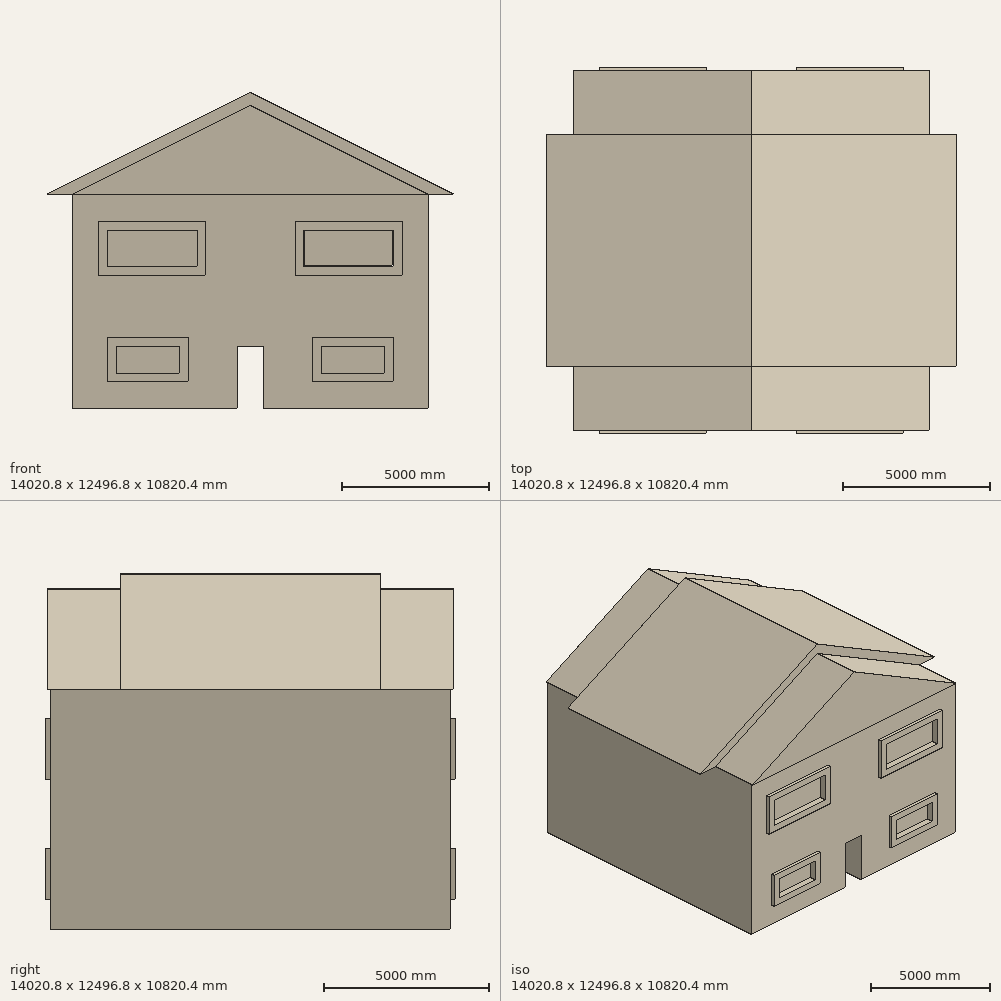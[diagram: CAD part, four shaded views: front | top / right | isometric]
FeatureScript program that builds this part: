
annotation { "Feature Type Name" : "Feature", "Feature Type Description" : "" }
export const myFeature = defineFeature(function(context is Context, id is Id, definition is map)
    precondition{}
    {
        {
            var Q0;
            Q0=qCreatedBy(makeId("Front.planeOp"),FACE);
            var sketch = newSketch(context, id + "F0", { "sketchPlane" : qUnion([Q0])});
            skLineSegment(sketch, "E0", {"start": v(0, 0) * mm, "end": v(-6096, 0) * mm});
            skLineSegment(sketch, "E1", {"start": v(0, 0) * mm, "end": v(6096, 0) * mm});
            skLineSegment(sketch, "E2", {"start": v(0, 0) * mm, "end": v(0, 3048) * mm, "construction": true});
            skLineSegment(sketch, "E3", {"start": v(0, 3048) * mm, "end": v(-6096, 0) * mm});
            skLineSegment(sketch, "E4", {"start": v(0, 3048) * mm, "end": v(6096, 0) * mm});
            skLineSegment(sketch, "E5", {"start": v(-6096, 0) * mm, "end": v(-7010.4, 0) * mm});
            skLineSegment(sketch, "E6", {"start": v(6096, 0) * mm, "end": v(7010.4, 0) * mm});
            skLineSegment(sketch, "E7", {"start": v(0, 3048) * mm, "end": v(0, 3505.2) * mm});
            skLineSegment(sketch, "E8", {"start": v(-7010.4, 0) * mm, "end": v(0, 3505.2) * mm});
            skLineSegment(sketch, "E9", {"start": v(0, 3505.2) * mm, "end": v(7010.4, 0) * mm});
            skLineSegment(sketch, "E10", {"start": v(-6096, 0) * mm, "end": v(-6096, -7315.2) * mm});
            skLineSegment(sketch, "E11", {"start": v(6096, 0) * mm, "end": v(6096, -7315.2) * mm});
            skLineSegment(sketch, "E12", {"start": v(-6096, -7315.2) * mm, "end": v(6096, -7315.2) * mm});
            skLineSegment(sketch, "E13", {"start": v(0, 0) * mm, "end": v(0, -7315.2) * mm, "construction": true});
            skLineSegment(sketch, "E14", {"start": v(0, -7315.2) * mm, "end": v(-457.2, -7315.2) * mm});
            skLineSegment(sketch, "E15", {"start": v(0, -7315.2) * mm, "end": v(457.2, -7315.2) * mm});
            skLineSegment(sketch, "E16", {"start": v(-457.2, -7315.2) * mm, "end": v(-457.2, -5181.6) * mm});
            skLineSegment(sketch, "E17", {"start": v(457.2, -7315.2) * mm, "end": v(457.2, -5181.6) * mm});
            skLineSegment(sketch, "E18", {"start": v(-457.2, -5181.6) * mm, "end": v(457.2, -5181.6) * mm});
            skPoint(sketch, "E19.firstSnap0", {"position": v(0, -5181.6) * mm});
            skLineSegment(sketch, "E19.bottom", {"start": v(2438.4, -5181.6) * mm, "end": v(4572, -5181.6) * mm});
            skLineSegment(sketch, "E19.top", {"start": v(2438.4, -6096) * mm, "end": v(4572, -6096) * mm});
            skLineSegment(sketch, "E19.left", {"start": v(2438.4, -5181.6) * mm, "end": v(2438.4, -6096) * mm});
            skLineSegment(sketch, "E19.right", {"start": v(4572, -5181.6) * mm, "end": v(4572, -6096) * mm});
            skLineSegment(sketch, "E20", {"start": v(-6096, -7315.2) * mm, "end": v(-6096, -7620) * mm});
            skLineSegment(sketch, "E21", {"start": v(6096, -7315.2) * mm, "end": v(6096, -7620) * mm});
            skLineSegment(sketch, "E22", {"start": v(6096, -7620) * mm, "end": v(-6096, -7620) * mm});
            skLineSegment(sketch, "E23.0", {"start": v(2133.6, -4876.8) * mm, "end": v(4876.8, -4876.8) * mm});
            skLineSegment(sketch, "E23.1", {"start": v(2133.6, -4876.8) * mm, "end": v(2133.6, -6400.8) * mm});
            skLineSegment(sketch, "E23.2", {"start": v(2133.6, -6400.8) * mm, "end": v(4876.8, -6400.8) * mm});
            skLineSegment(sketch, "E23.3", {"start": v(4876.8, -4876.8) * mm, "end": v(4876.8, -6400.8) * mm});
            skLineSegment(sketch, "E24.bottom", {"start": v(-4572, -5181.6) * mm, "end": v(-2438.4, -5181.6) * mm});
            skLineSegment(sketch, "E24.top", {"start": v(-4572, -6096) * mm, "end": v(-2438.4, -6096) * mm});
            skLineSegment(sketch, "E24.left", {"start": v(-4572, -5181.6) * mm, "end": v(-4572, -6096) * mm});
            skLineSegment(sketch, "E24.right", {"start": v(-2438.4, -5181.6) * mm, "end": v(-2438.4, -6096) * mm});
            skLineSegment(sketch, "E25.0", {"start": v(-4876.8, -4876.8) * mm, "end": v(-2133.6, -4876.8) * mm});
            skLineSegment(sketch, "E25.1", {"start": v(-4876.8, -4876.8) * mm, "end": v(-4876.8, -6400.8) * mm});
            skLineSegment(sketch, "E25.2", {"start": v(-4876.8, -6400.8) * mm, "end": v(-2133.6, -6400.8) * mm});
            skLineSegment(sketch, "E25.3", {"start": v(-2133.6, -4876.8) * mm, "end": v(-2133.6, -6400.8) * mm});
            skLineSegment(sketch, "E26.bottom", {"start": v(1828.8, -1219.2) * mm, "end": v(4876.8, -1219.2) * mm});
            skLineSegment(sketch, "E26.top", {"start": v(1828.8, -2438.4) * mm, "end": v(4876.8, -2438.4) * mm});
            skLineSegment(sketch, "E26.left", {"start": v(1828.8, -1219.2) * mm, "end": v(1828.8, -2438.4) * mm});
            skLineSegment(sketch, "E26.right", {"start": v(4876.8, -1219.2) * mm, "end": v(4876.8, -2438.4) * mm});
            skLineSegment(sketch, "E27.0", {"start": v(1833.8, -1219.2) * mm, "end": v(1833.8, -2433.4) * mm});
            skLineSegment(sketch, "E27.1", {"start": v(1833.8, -2433.4) * mm, "end": v(4871.8, -2433.4) * mm});
            skLineSegment(sketch, "E27.2", {"start": v(4871.8, -1219.2) * mm, "end": v(4871.8, -2433.4) * mm});
            skLineSegment(sketch, "E28.0", {"start": v(1828.8, -1224.2) * mm, "end": v(4876.8, -1224.2) * mm});
            skLineSegment(sketch, "E29.bottom", {"start": v(-4876.8, -1219.2) * mm, "end": v(-1828.8, -1219.2) * mm});
            skLineSegment(sketch, "E29.top", {"start": v(-4876.8, -2438.4) * mm, "end": v(-1828.8, -2438.4) * mm});
            skLineSegment(sketch, "E29.left", {"start": v(-4876.8, -1219.2) * mm, "end": v(-4876.8, -2438.4) * mm});
            skLineSegment(sketch, "E29.right", {"start": v(-1828.8, -1219.2) * mm, "end": v(-1828.8, -2438.4) * mm});
            skLineSegment(sketch, "E30.0", {"start": v(-5181.6, -914.4) * mm, "end": v(-1524, -914.4) * mm});
            skLineSegment(sketch, "E30.1", {"start": v(-5181.6, -914.4) * mm, "end": v(-5181.6, -2743.2) * mm});
            skLineSegment(sketch, "E30.2", {"start": v(-5181.6, -2743.2) * mm, "end": v(-1524, -2743.2) * mm});
            skLineSegment(sketch, "E30.3", {"start": v(-1524, -914.4) * mm, "end": v(-1524, -2743.2) * mm});
            skLineSegment(sketch, "E31.0", {"start": v(1524, -914.4) * mm, "end": v(5181.6, -914.4) * mm});
            skLineSegment(sketch, "E31.1", {"start": v(1524, -914.4) * mm, "end": v(1524, -2743.2) * mm});
            skLineSegment(sketch, "E31.2", {"start": v(1524, -2743.2) * mm, "end": v(5181.6, -2743.2) * mm});
            skLineSegment(sketch, "E31.3", {"start": v(5181.6, -914.4) * mm, "end": v(5181.6, -2743.2) * mm});
            skSolve(sketch);
        }
        {
            var Q0;
            Q0=makeQuery(id+"F0.imprint","IMPRINT",FACE,{"disambiguationData":[TD([[makeQuery(id+"F0.imprint","IMPRINT",EDGE,{"derivedFrom":sQuery(id+"F0.wireOp",EDGE,"E3")}),-1.0]])]});
            var Q1;
            Q1=makeQuery(id+"F0.imprint","IMPRINT",FACE,{"disambiguationData":[TD([[makeQuery(id+"F0.imprint","IMPRINT",EDGE,{"derivedFrom":sQuery(id+"F0.wireOp",EDGE,"E4")}),1.0]])]});
            extrude(context, id + "F1", {"entities" : qUnion([Q0, Q1]), "endBound" : BoundingType.SYMMETRIC, "depth" : 7924.8 * mm, "offsetDistance" : 30.48 * mm});
        }
        {
            var Q0;
            Q0=makeQuery(id+"F0.imprint","IMPRINT",FACE,{"disambiguationData":[TD([[makeQuery(id+"F0.imprint","IMPRINT",EDGE,{"derivedFrom":sQuery(id+"F0.wireOp",EDGE,"E0")}),-1.0]])]});
            extrude(context, id + "F2", {"entities" : qUnion([Q0]), "operationType" : NewBodyOperationType.ADD, "endBound" : BoundingType.SYMMETRIC, "depth" : 12344.4 * mm, "offsetDistance" : 30.48 * mm});
        }
        {
            var Q0;
            Q0=makeQuery(id+"F0.imprint","IMPRINT",FACE,{"disambiguationData":[TD([[makeQuery(id+"F0.imprint","IMPRINT",EDGE,{"derivedFrom":sQuery(id+"F0.wireOp",EDGE,"E0")}),1.0]])]});
            extrude(context, id + "F3", {"entities" : qUnion([Q0]), "operationType" : NewBodyOperationType.ADD, "endBound" : BoundingType.SYMMETRIC, "depth" : 12192 * mm, "offsetDistance" : 30.48 * mm});
        }
        {
            var Q0;
            {var subQ0=sQuery(id+"F0.wireOp",EDGE,"E27.1");Q0=makeQuery(id+"F0.imprint","IMPRINT",FACE,{"disambiguationData":[TD([[makeQuery(id+"F0.imprint","IMPRINT",EDGE,{"derivedFrom":subQ0}),1.0]])]});}
            var Q1;
            Q1=makeQuery(id+"F0.imprint","IMPRINT",FACE,{"disambiguationData":[TD([[makeQuery(id+"F0.imprint","IMPRINT",EDGE,{"derivedFrom":sQuery(id+"F0.wireOp",EDGE,"E19.bottom")}),-1.0]])]});
            var Q2;
            Q2=makeQuery(id+"F0.imprint","IMPRINT",FACE,{"disambiguationData":[TD([[makeQuery(id+"F0.imprint","IMPRINT",EDGE,{"derivedFrom":sQuery(id+"F0.wireOp",EDGE,"E29.bottom")}),-1.0]])]});
            var Q3;
            Q3=makeQuery(id+"F0.imprint","IMPRINT",FACE,{"disambiguationData":[TD([[makeQuery(id+"F0.imprint","IMPRINT",EDGE,{"derivedFrom":sQuery(id+"F0.wireOp",EDGE,"E24.bottom")}),-1.0]])]});
            extrude(context, id + "F4", {"entities" : qUnion([Q0, Q1, Q2, Q3]), "endBound" : BoundingType.SYMMETRIC, "depth" : 11887.2 * mm, "offsetDistance" : 30.48 * mm});
        }
        {
            var Q0;
            Q0=makeQuery(id+"F0.imprint","IMPRINT",FACE,{"disambiguationData":[TD([[makeQuery(id+"F0.imprint","IMPRINT",EDGE,{"derivedFrom":sQuery(id+"F0.wireOp",EDGE,"E14")}),-1.0]])]});
            var Q1;
            Q1=makeQuery(id+"F0.imprint","IMPRINT",FACE,{"disambiguationData":[TD([[makeQuery(id+"F0.imprint","IMPRINT",EDGE,{"derivedFrom":sQuery(id+"F0.wireOp",EDGE,"E24.bottom")}),1.0]])]});
            var Q2;
            Q2=makeQuery(id+"F0.imprint","IMPRINT",FACE,{"disambiguationData":[TD([[makeQuery(id+"F0.imprint","IMPRINT",EDGE,{"derivedFrom":sQuery(id+"F0.wireOp",EDGE,"E29.bottom")}),1.0]])]});
            var Q3;
            {var subQ1=sQuery(id+"F0.wireOp",EDGE,"E26.top");Q3=makeQuery(id+"F0.imprint","IMPRINT",FACE,{"disambiguationData":[TD([[makeQuery(id+"F0.imprint","IMPRINT",EDGE,{"derivedFrom":subQ1}),-1.0]])]});}
            var Q4;
            Q4=makeQuery(id+"F0.imprint","IMPRINT",FACE,{"disambiguationData":[TD([[makeQuery(id+"F0.imprint","IMPRINT",EDGE,{"derivedFrom":sQuery(id+"F0.wireOp",EDGE,"E19.bottom")}),1.0]])]});
            extrude(context, id + "F5", {"entities" : qUnion([Q0, Q1, Q2, Q3, Q4]), "endBound" : BoundingType.SYMMETRIC, "depth" : 12496.8 * mm, "offsetDistance" : 30.48 * mm});
        }
    });
